# Revit family: Sink-45cm-WithOverflowHole-Vitra-ArkitektSeries-6109
name_source: partatom
category: Plumbing Fixtures
revit_build: Autodesk Revit 2017 (Build: 20160225_1515(x64)
units: mm (PartAtom-declared; Revit-internal decimal feet)

## family parameters
Cut with Voids When Loaded = No
Host = Face
OmniClass Number = 23.45.05.14.14
OmniClass Title = Sinks/Lavatories
Part Type = Normal
Room Calculation Point = No
Round Connector Dimension = Use Diameter
Shared = Yes

## types (4) — shared parameters
BIMobject category = Kitchen - Sinks
Brand = VitrA
CW Connection = No
Color = White
Default Elevation = 850 mm  [stored 2.78871 ft]
Design country = Turkey
HW Connection = No
IFC Classification = Sanitary Terminal
Main Material = Ceramic
Manufacturer = Vitra
Manufacturer name = Vitra
Masterformat 2014 Code = 22 40 00
Masterformat 2014 Description = Plumbing Fixtures
Mounting type = Wall Hung
NBS Referans Code = 31-79
NBS Referans Description = Wash basins, sinks and troughs
Nominal Depth (mm) = 340 mm  [stored 1.11549 ft]
Nominal Height (mm) = 350 mm  [stored 1.14829 ft]
Nominal Width (mm) = 460 mm  [stored 1.50919 ft]
OmniClass Code = 23.45.05.14.14
OmniClass Description = Sinks/Lavatories
Primary Material = White
Product certification = https://www.vitraglobal.com
Product family = Wall Mounted Sink
Product group = Arkitekt
Product url = https://www.vitraglobal.com
Technical description = https://www.vitraglobal.com
UNSPSC Description = Sinks
URL = https://vitraglobal.com
Uniclass 1.4 Code = L7232
Uniclass 1.4 Description = Sinks for kitchens, bars
Uniclass 2.0 Code = PR-31-79
Uniclass 2.0 Description = Sinks, Wash Basins And Troughs
Uniclass 2015 Code = Pr_40_20_96
Uniclass 2015 Name = Wash basins, Sinks and troughs
Uniformat II Code = D2010
Uniformat II Description = Plumbing Fixtures
Vent Connection = No
Warranty Period (Year) = 10 Years
Waste Connection = Yes
Weight Net (kg) = 16.6
Youtube = https://www.youtube.com

## per-type parameters (varying)
| type | Article No. (default) | Description | Model | Product SKU | Product data url |
| Sink_45cm_WithOverflowHole_Vitra_ArkitektSeries_6109B003-6105 | 6109B003-6105 | VitrA Arkitekt Sink, With Overflow Hole | 6109B003-6105 | 6109B003-6105 |  |
| Sink_45cm_WithOverflowHole_Vitra_ArkitektSeries_6109B003-6005 | 6109B003-6005 | VitrA Arkitekt Sink, With Overflow Hole | 6109B003-6005 | 6109B003-6005 |  |
| Sink_45cm_WithOverflowHole_Vitra_ArkitektSeries_6109B003-0016 | 6109B003-0016 | VitrA Arkitekt Sink, With Overflow Hole | 6109B003-0016 | 6109B003-0016 |  |
| Sink_45cm_WithOverflowHole_Vitra_ArkitektSeries_6109B003-0012 | 6109B003-0012 | VitrA Arkitekt Sink - With Overflow Hole | 6109B003-0012 | 6109B003-0012 | https://www.bimobject.com |

note: [stored X ft] marks values corroborated as IEEE doubles in the binary element streams (Revit-internal decimal feet)

## geometry (parser evidence)
native form markers: Sweep x2
no freeform markers — native parametric forms only
